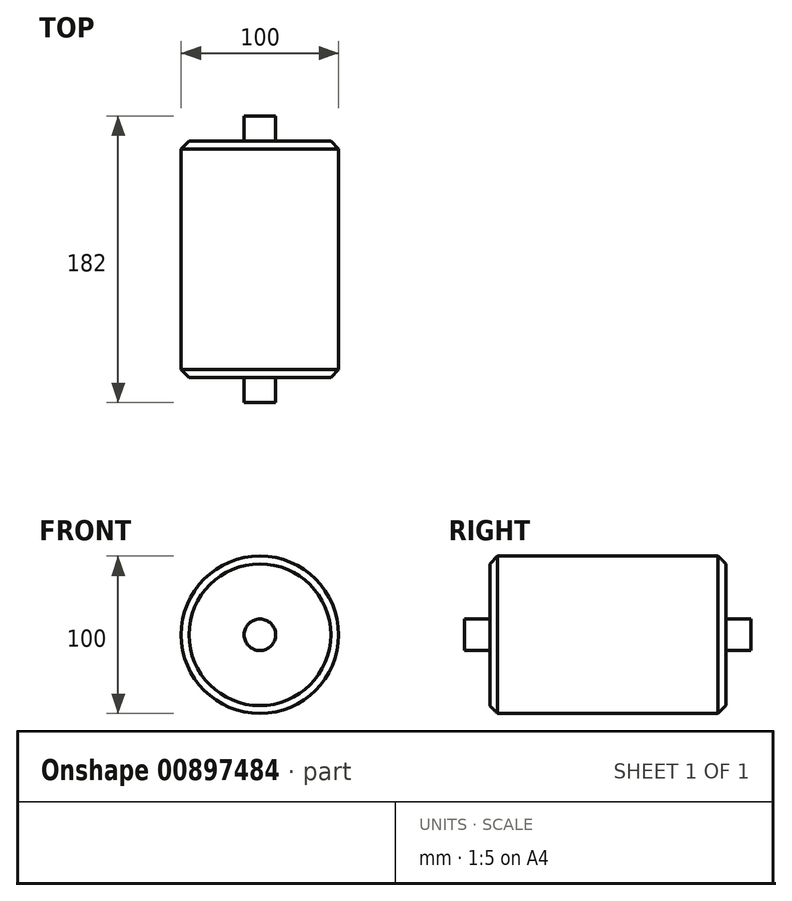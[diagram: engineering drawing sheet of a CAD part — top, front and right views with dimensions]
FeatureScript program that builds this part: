
annotation { "Feature Type Name" : "Feature", "Feature Type Description" : "" }
export const myFeature = defineFeature(function(context is Context, id is Id, definition is map)
    precondition{}
    {
        {
            var Q0;
            Q0=qCreatedBy(makeId("Front.planeOp"),FACE);
            var sketch = newSketch(context, id + "F0", { "sketchPlane" : qUnion([Q0])});
            skCircle(sketch, "E0", {"center": v(0, 0) * mm, "radius": 50 * mm});
            skSolve(sketch);
        }
        {
            var Q0;
            Q0 = qSketchRegion(id + "F0", true);
            extrude(context, id + "F1", {"entities" : qUnion([Q0]), "depth" : 75 * mm, "offsetDistance" : 25.4 * mm});
        }
        {
            var Q0;
            Q0=makeQuery(id+"F1.opExtrude","CAP_FACE",FACE,{"disambiguationData":[OSD([sQuery(id+"F0.wireOp",EDGE,"E0")])],"isStart":true});
            var sketch = newSketch(context, id + "F2", { "sketchPlane" : qUnion([Q0])});
            skSolve(sketch);
        }
        {
            var Q0;
            Q0=makeQuery(id+"F2.imprint","IMPRINT",FACE,{"disambiguationData":[TD([[makeQuery(id+"F2.imprint","IMPRINT",EDGE,{"derivedFrom":makeQuery(id+"F1.opExtrude","CAP_EDGE",EDGE,{"disambiguationData":[OSD([sQuery(id+"F0.wireOp",EDGE,"E0")])],"isStart":true})}),-1.0]])]});
            extrude(context, id + "F3", {"entities" : qUnion([Q0]), "operationType" : NewBodyOperationType.ADD, "depth" : 75 * mm, "offsetDistance" : 25.4 * mm});
        }
        {
            var Q0;
            Q0=makeQuery(id+"F1.opExtrude","CAP_FACE",FACE,{"disambiguationData":[OSD([sQuery(id+"F0.wireOp",EDGE,"E0")])],"isStart":false});
            var sketch = newSketch(context, id + "F4", { "sketchPlane" : qUnion([Q0])});
            skCircle(sketch, "E1", {"center": v(0, 0) * mm, "radius": 10 * mm});
            skSolve(sketch);
        }
        {
            var Q0;
            Q0 = qSketchRegion(id + "F4", true);
            extrude(context, id + "F5", {"entities" : qUnion([Q0]), "operationType" : NewBodyOperationType.ADD, "depth" : 16 * mm, "offsetDistance" : 25.4 * mm});
        }
        {
            var Q0;
            Q0=makeQuery(id+"F3.opExtrude","CAP_FACE",FACE,{"disambiguationData":[OSD([sQuery(id+"F0.wireOp",EDGE,"E0")])],"isStart":false});
            var sketch = newSketch(context, id + "F6", { "sketchPlane" : qUnion([Q0])});
            skCircle(sketch, "E2", {"center": v(0, 0) * mm, "radius": 10 * mm});
            skSolve(sketch);
        }
        {
            var Q0;
            Q0=makeQuery(id+"F6.imprint","IMPRINT",FACE,{"disambiguationData":[TD([[makeQuery(id+"F6.imprint","IMPRINT",EDGE,{"derivedFrom":sQuery(id+"F6.wireOp",EDGE,"E2")}),1.0]])]});
            extrude(context, id + "F7", {"entities" : qUnion([Q0]), "operationType" : NewBodyOperationType.ADD, "depth" : 16 * mm, "offsetDistance" : 25.4 * mm});
        }
        {
            var Q0;
            Q0=makeQuery(id+"F1.opExtrude","CAP_EDGE",EDGE,{"disambiguationData":[OSD([sQuery(id+"F0.wireOp",EDGE,"E0")])],"isStart":false});
            chamfer(context, id + "F8", {"entities" : qUnion([Q0]), "chamferType" : ChamferType.OFFSET_ANGLE, "width" : 5 * mm, "oppositeDirection" : false, "angle" : 45 * degree, "tangentPropagation" : true});
        }
        {
            var Q0;
            Q0=makeQuery(id+"F3.opExtrude","CAP_EDGE",EDGE,{"disambiguationData":[OSD([sQuery(id+"F0.wireOp",EDGE,"E0")])],"isStart":false});
            chamfer(context, id + "F9", {"entities" : qUnion([Q0]), "chamferType" : ChamferType.OFFSET_ANGLE, "width" : 5 * mm, "oppositeDirection" : false, "angle" : 45 * degree, "tangentPropagation" : true});
        }
    });
